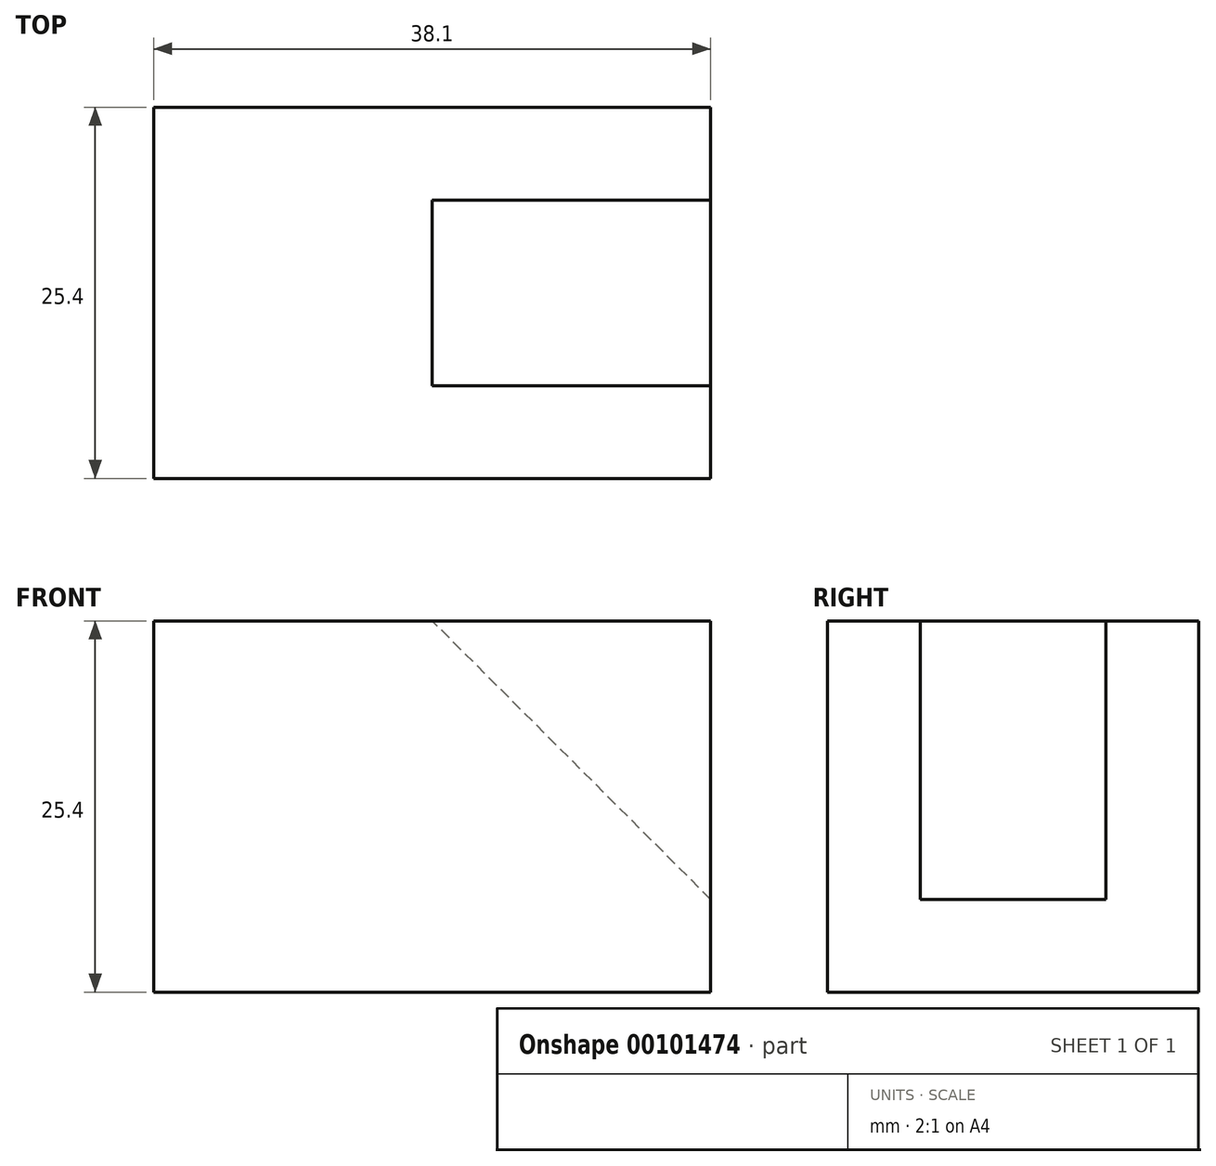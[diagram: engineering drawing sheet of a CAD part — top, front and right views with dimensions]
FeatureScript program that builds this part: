
annotation { "Feature Type Name" : "Feature", "Feature Type Description" : "" }
export const myFeature = defineFeature(function(context is Context, id is Id, definition is map)
    precondition{}
    {
        {
            var Q0;
            Q0=qCreatedBy(makeId("Front.planeOp"),FACE);
            var sketch = newSketch(context, id + "F0", { "sketchPlane" : qUnion([Q0])});
            skLineSegment(sketch, "E0", {"start": v(0, 0) * mm, "end": v(0, 25.4) * mm});
            skLineSegment(sketch, "E1", {"start": v(0, 25.4) * mm, "end": v(38.1, 25.4) * mm});
            skLineSegment(sketch, "E2", {"start": v(38.1, 25.4) * mm, "end": v(38.1, 0) * mm});
            skLineSegment(sketch, "E3", {"start": v(38.1, 0) * mm, "end": v(0, 0) * mm});
            skLineSegment(sketch, "E4", {"start": v(38.1, 25.4) * mm, "end": v(38.1, 6.35) * mm});
            skLineSegment(sketch, "E5", {"start": v(38.1, 6.35) * mm, "end": v(19.05, 25.4) * mm});
            skLineSegment(sketch, "E6", {"start": v(19.05, 25.4) * mm, "end": v(38.1, 25.4) * mm});
            skSolve(sketch);
        }
        {
            var Q0;
            Q0=qCreatedBy(makeId("Right.planeOp"),FACE);
            var sketch = newSketch(context, id + "F1", { "sketchPlane" : qUnion([Q0])});
            skLineSegment(sketch, "E7", {"start": v(0, 0) * mm, "end": v(0, 25.4) * mm});
            skLineSegment(sketch, "E8", {"start": v(0, 25.4) * mm, "end": v(25.4, 25.4) * mm});
            skLineSegment(sketch, "E9", {"start": v(25.4, 25.4) * mm, "end": v(25.4, 0) * mm});
            skLineSegment(sketch, "E10", {"start": v(25.4, 0) * mm, "end": v(0, 0) * mm});
            skSolve(sketch);
        }
        {
            var Q0;
            Q0=makeQuery(id+"F0.imprint","IMPRINT",FACE,{"disambiguationData":[TD([[makeQuery(id+"F0.imprint","IMPRINT",EDGE,{"derivedFrom":sQuery(id+"F0.wireOp",EDGE,"E0")}),-1.0]])]});
            extrude(context, id + "F2", {"entities" : qUnion([Q0]), "oppositeDirection" : true, "depth" : 25.4 * mm});
        }
        {
            var Q0;
            Q0=qCreatedBy(makeId("Top.planeOp"),FACE);
            var sketch = newSketch(context, id + "F3", { "sketchPlane" : qUnion([Q0])});
            skLineSegment(sketch, "E11", {"start": v(0, 0) * mm, "end": v(0, 25.4) * mm});
            skLineSegment(sketch, "E12", {"start": v(0, 25.4) * mm, "end": v(38.1, 25.4) * mm});
            skLineSegment(sketch, "E13", {"start": v(38.1, 25.4) * mm, "end": v(38.1, 19.05) * mm});
            skLineSegment(sketch, "E14", {"start": v(38.1, 19.05) * mm, "end": v(19.05, 19.05) * mm});
            skLineSegment(sketch, "E15", {"start": v(19.05, 19.05) * mm, "end": v(19.05, 6.35) * mm});
            skLineSegment(sketch, "E16", {"start": v(19.05, 6.35) * mm, "end": v(38.1, 6.35) * mm});
            skLineSegment(sketch, "E17", {"start": v(38.1, 6.35) * mm, "end": v(38.1, 0) * mm});
            skLineSegment(sketch, "E18", {"start": v(38.1, 0) * mm, "end": v(0, 0) * mm});
            skSolve(sketch);
        }
        {
            var Q0;
            Q0=makeQuery(id+"F3.imprint","IMPRINT",FACE,{"disambiguationData":[TD([[makeQuery(id+"F3.imprint","IMPRINT",EDGE,{"derivedFrom":sQuery(id+"F3.wireOp",EDGE,"E11")}),-1.0]])]});
            extrude(context, id + "F4", {"entities" : qUnion([Q0]), "operationType" : NewBodyOperationType.ADD, "depth" : 25.4 * mm});
        }
    });
